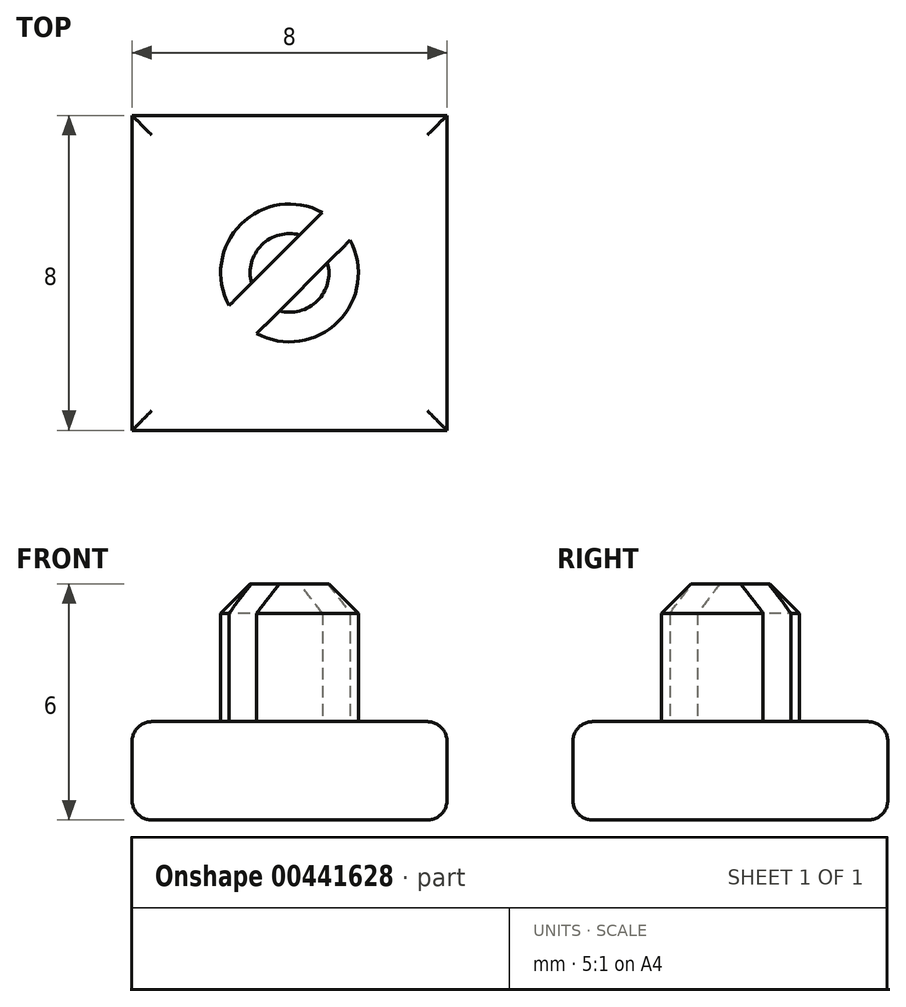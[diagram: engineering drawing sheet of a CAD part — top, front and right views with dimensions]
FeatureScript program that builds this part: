
annotation { "Feature Type Name" : "Feature", "Feature Type Description" : "" }
export const myFeature = defineFeature(function(context is Context, id is Id, definition is map)
    precondition{}
    {
        {
            var Q0;
            Q0=qCreatedBy(makeId("Top.planeOp"),FACE);
            var sketch = newSketch(context, id + "F0", { "sketchPlane" : qUnion([Q0])});
            skLineSegment(sketch, "E0.bottom", {"start": v(0, 0) * mm, "end": v(8, 0) * mm});
            skLineSegment(sketch, "E0.top", {"start": v(0, 8) * mm, "end": v(8, 8) * mm});
            skLineSegment(sketch, "E0.left", {"start": v(0, 0) * mm, "end": v(0, 8) * mm});
            skLineSegment(sketch, "E0.right", {"start": v(8, 0) * mm, "end": v(8, 8) * mm});
            skSolve(sketch);
        }
        {
            var Q0;
            Q0=makeQuery(id+"F0.imprint","IMPRINT",FACE,{"disambiguationData":[TD([[makeQuery(id+"F0.imprint","IMPRINT",EDGE,{"derivedFrom":sQuery(id+"F0.wireOp",EDGE,"E0.bottom")}),1.0]])]});
            extrude(context, id + "F1", {"entities" : qUnion([Q0]), "depth" : 2.5 * mm});
        }
        {
            var Q0;
            Q0=makeQuery(id+"F1.opExtrude","CAP_FACE",FACE,{"disambiguationData":[OSD([sQuery(id+"F0.wireOp",EDGE,"E0.bottom"),sQuery(id+"F0.wireOp",EDGE,"E0.top"),sQuery(id+"F0.wireOp",EDGE,"E0.left"),sQuery(id+"F0.wireOp",EDGE,"E0.right")])],"isStart":false});
            var sketch = newSketch(context, id + "F2", { "sketchPlane" : qUnion([Q0])});
            skLineSegment(sketch, "E1.0.0", {"start": v(8, 8) * mm, "end": v(0, 8) * mm});
            skLineSegment(sketch, "E1.0.1", {"start": v(0, 8) * mm, "end": v(0, 0) * mm});
            skLineSegment(sketch, "E1.0.2", {"start": v(0, 0) * mm, "end": v(8, 0) * mm});
            skLineSegment(sketch, "E1.0.3", {"start": v(8, 0) * mm, "end": v(8, 8) * mm});
            skLineSegment(sketch, "E2", {"start": v(8, 8) * mm, "end": v(0, 0) * mm, "construction": true});
            skCircle(sketch, "E3", {"center": v(4, 4) * mm, "radius": 1.75 * mm});
            skLineSegment(sketch, "E4", {"start": v(2.46, 3.17) * mm, "end": v(4.83, 5.54) * mm});
            skLineSegment(sketch, "E5", {"start": v(3.17, 2.46) * mm, "end": v(5.54, 4.83) * mm});
            skSolve(sketch);
        }
        {
            var Q0;
            {var subQ0=sQuery(id+"F2.wireOp",EDGE,"E4");Q0=makeQuery(id+"F2.imprint","IMPRINT",FACE,{"disambiguationData":[TD([[makeQuery(id+"F2.imprint","IMPRINT",EDGE,{"derivedFrom":subQ0}),1.0]])]});}
            var Q1;
            {var subQ0=sQuery(id+"F2.wireOp",EDGE,"E5");Q1=makeQuery(id+"F2.imprint","IMPRINT",FACE,{"disambiguationData":[TD([[makeQuery(id+"F2.imprint","IMPRINT",EDGE,{"derivedFrom":subQ0}),-1.0]])]});}
            extrude(context, id + "F3", {"entities" : qUnion([Q0, Q1]), "operationType" : NewBodyOperationType.ADD, "depth" : 3.5 * mm});
        }
        {
            var Q0;
            {var subQ0=sQuery(id+"F2.wireOp",EDGE,"E5");var subQ1=sQuery(id+"F2.wireOp",EDGE,"E3");Q0=makeQuery(id+"F3.opExtrude","CAP_EDGE",EDGE,{"disambiguationData":[OSD([subQ1]),TDD([makeQuery(id+"F2.imprint","IMPRINT",EDGE,{"disambiguationData":[TD([[makeQuery(id+"F2.imprint","INTERSECT",VERTEX,{"disambiguationData":[OD(0.0)],"derivedFrom":[subQ1,subQ0]}),-1.0]])],"derivedFrom":subQ1})])],"isStart":false});}
            var Q1;
            {var subQ0=sQuery(id+"F2.wireOp",EDGE,"E4");var subQ1=sQuery(id+"F2.wireOp",EDGE,"E3");Q1=makeQuery(id+"F3.opExtrude","CAP_EDGE",EDGE,{"disambiguationData":[OSD([subQ1]),TDD([makeQuery(id+"F2.imprint","IMPRINT",EDGE,{"disambiguationData":[TD([[makeQuery(id+"F2.imprint","INTERSECT",VERTEX,{"disambiguationData":[OD(0.0)],"derivedFrom":[subQ1,subQ0]}),1.0]])],"derivedFrom":subQ1})])],"isStart":false});}
            chamfer(context, id + "F4", {"entities" : qUnion([Q0, Q1]), "width" : .75 * mm, "tangentPropagation" : true});
        }
        {
            var Q0;
            Q0=makeQuery(id+"F1.opExtrude","CAP_EDGE",EDGE,{"disambiguationData":[OSD([sQuery(id+"F0.wireOp",EDGE,"E0.left")])],"isStart":false});
            var Q1;
            Q1=makeQuery(id+"F1.opExtrude","CAP_EDGE",EDGE,{"disambiguationData":[OSD([sQuery(id+"F0.wireOp",EDGE,"E0.bottom")])],"isStart":false});
            var Q2;
            Q2=makeQuery(id+"F1.opExtrude","CAP_EDGE",EDGE,{"disambiguationData":[OSD([sQuery(id+"F0.wireOp",EDGE,"E0.right")])],"isStart":false});
            var Q3;
            Q3=makeQuery(id+"F1.opExtrude","CAP_EDGE",EDGE,{"disambiguationData":[OSD([sQuery(id+"F0.wireOp",EDGE,"E0.top")])],"isStart":false});
            var Q4;
            Q4=makeQuery(id+"F1.opExtrude","CAP_EDGE",EDGE,{"disambiguationData":[OSD([sQuery(id+"F0.wireOp",EDGE,"E0.top")])],"isStart":true});
            var Q5;
            Q5=makeQuery(id+"F1.opExtrude","CAP_EDGE",EDGE,{"disambiguationData":[OSD([sQuery(id+"F0.wireOp",EDGE,"E0.right")])],"isStart":true});
            var Q6;
            Q6=makeQuery(id+"F1.opExtrude","CAP_EDGE",EDGE,{"disambiguationData":[OSD([sQuery(id+"F0.wireOp",EDGE,"E0.bottom")])],"isStart":true});
            var Q7;
            Q7=makeQuery(id+"F1.opExtrude","CAP_EDGE",EDGE,{"disambiguationData":[OSD([sQuery(id+"F0.wireOp",EDGE,"E0.left")])],"isStart":true});
            fillet(context, id + "F5", {"entities" : qUnion([Q0, Q1, Q2, Q3, Q4, Q5, Q6, Q7]), "radius" : .5 * mm, "tangentPropagation" : true, "allowEdgeOverflow" : false});
        }
    });
